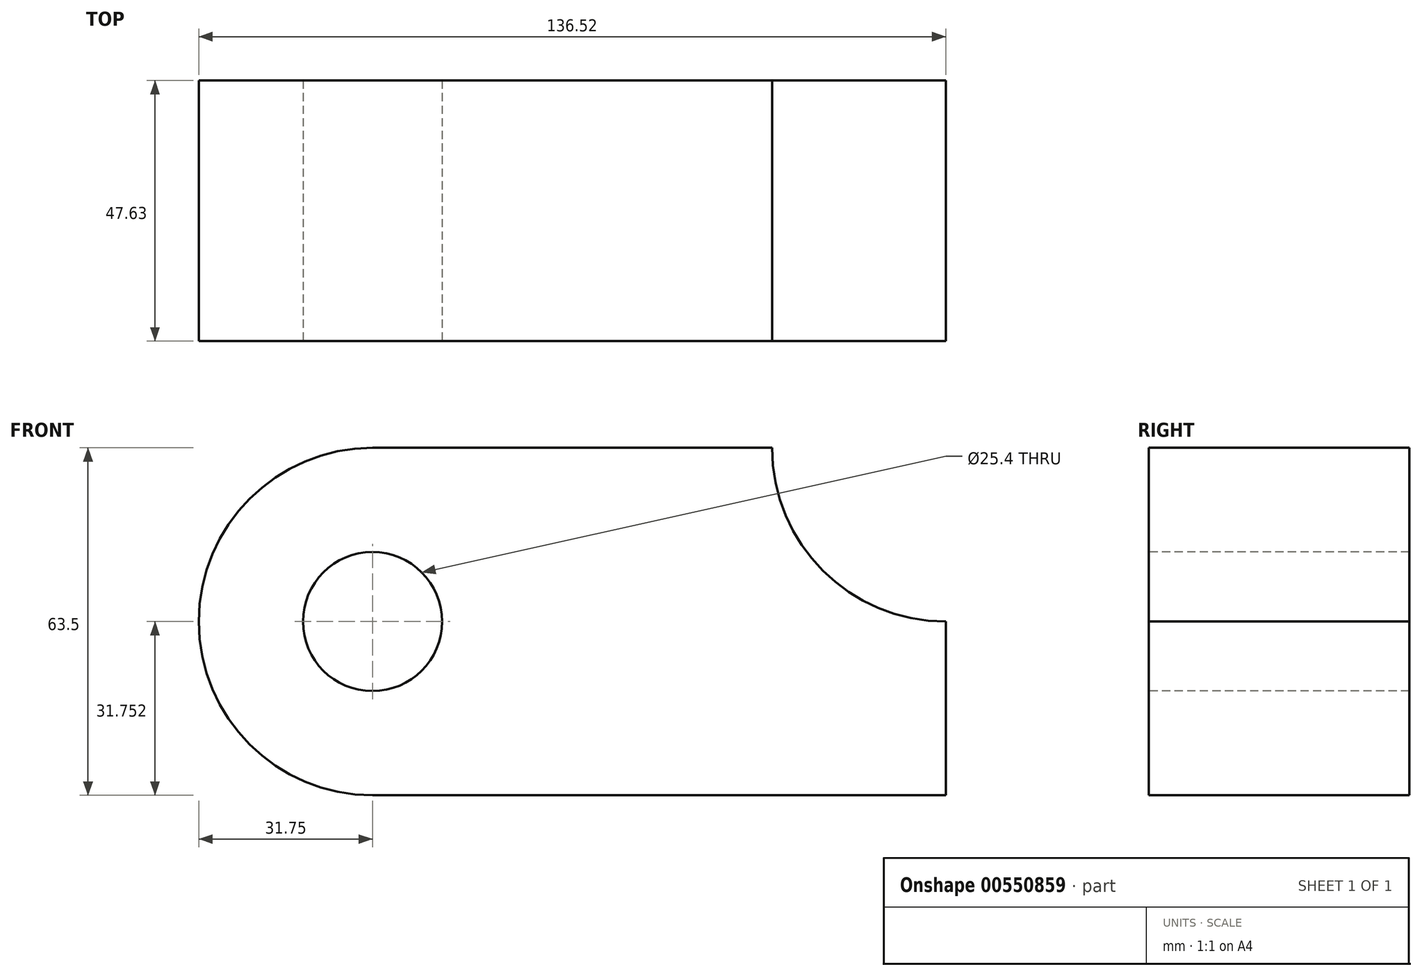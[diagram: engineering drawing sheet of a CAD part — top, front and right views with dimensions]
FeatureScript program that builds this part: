
annotation { "Feature Type Name" : "Feature", "Feature Type Description" : "" }
export const myFeature = defineFeature(function(context is Context, id is Id, definition is map)
    precondition{}
    {
        {
            var Q0;
            Q0=qCreatedBy(makeId("Front.planeOp"),FACE);
            var sketch = newSketch(context, id + "F0", { "sketchPlane" : qUnion([Q0])});
            skLineSegment(sketch, "E0.bottom", {"start": v(-34.63, 33.68) * mm, "end": v(70.14, 33.68) * mm});
            skLineSegment(sketch, "E0.top", {"start": v(-34.63, -29.82) * mm, "end": v(70.14, -29.82) * mm});
            skLineSegment(sketch, "E0.left", {"start": v(-34.63, 33.68) * mm, "end": v(-34.63, -29.82) * mm});
            skLineSegment(sketch, "E0.right", {"start": v(70.14, 33.68) * mm, "end": v(70.14, -29.82) * mm});
            skArc(sketch, "E1", {"start": v(-34.63, 33.68) * mm, "mid": v(-66.38, 1.93) * mm, "end": v(-34.63, -29.82) * mm});
            skSolve(sketch);
        }
        {
            var Q0;
            Q0 = qSketchRegion(id + "F0", true);
            extrude(context, id + "F1", {"entities" : qUnion([Q0]), "depth" : 47.62 * mm, "offsetDistance" : 25.4 * mm});
        }
        {
            var Q0;
            Q0=makeQuery(id+"F1.opExtrude","CAP_FACE",FACE,{"disambiguationData":[OSD([sQuery(id+"F0.wireOp",EDGE,"E0.bottom"),sQuery(id+"F0.wireOp",EDGE,"E0.top"),sQuery(id+"F0.wireOp",EDGE,"E0.right"),sQuery(id+"F0.wireOp",EDGE,"E1")])],"isStart":false});
            var sketch = newSketch(context, id + "F2", { "sketchPlane" : qUnion([Q0])});
            skCircle(sketch, "E2", {"center": v(-34.63, 1.93) * mm, "radius": 12.7 * mm});
            skPoint(sketch, "E2.centerSnap0", {"position": v(-66.38, 1.93) * mm});
            skSolve(sketch);
        }
        {
            var Q0;
            Q0=makeQuery(id+"F2.imprint","IMPRINT",FACE,{"disambiguationData":[TD([[makeQuery(id+"F2.imprint","IMPRINT",EDGE,{"derivedFrom":sQuery(id+"F2.wireOp",EDGE,"E2")}),1.0]])]});
            extrude(context, id + "F3", {"entities" : qUnion([Q0]), "operationType" : NewBodyOperationType.REMOVE, "oppositeDirection" : true, "depth" : 47.62 * mm, "offsetDistance" : 25.4 * mm});
        }
        {
            var Q0;
            Q0=makeQuery(id+"F1.opExtrude","CAP_FACE",FACE,{"disambiguationData":[OSD([sQuery(id+"F0.wireOp",EDGE,"E0.bottom"),sQuery(id+"F0.wireOp",EDGE,"E0.top"),sQuery(id+"F0.wireOp",EDGE,"E0.right"),sQuery(id+"F0.wireOp",EDGE,"E1")])],"isStart":false});
            var sketch = newSketch(context, id + "F4", { "sketchPlane" : qUnion([Q0])});
            skArc(sketch, "E3", {"start": v(38.4, 33.68) * mm, "mid": v(47.7, 11.23) * mm, "end": v(70.14, 1.93) * mm});
            skSolve(sketch);
        }
        {
            var Q0;
            {var subQ0=sQuery(id+"F4.wireOp",EDGE,"E3");Q0=makeQuery(id+"F4.imprint","IMPRINT",FACE,{"disambiguationData":[TD([[makeQuery(id+"F4.imprint","IMPRINT",EDGE,{"derivedFrom":subQ0}),1.0]])]});}
            extrude(context, id + "F5", {"entities" : qUnion([Q0]), "operationType" : NewBodyOperationType.REMOVE, "oppositeDirection" : true, "depth" : 47.62 * mm, "offsetDistance" : 25.4 * mm});
        }
    });
